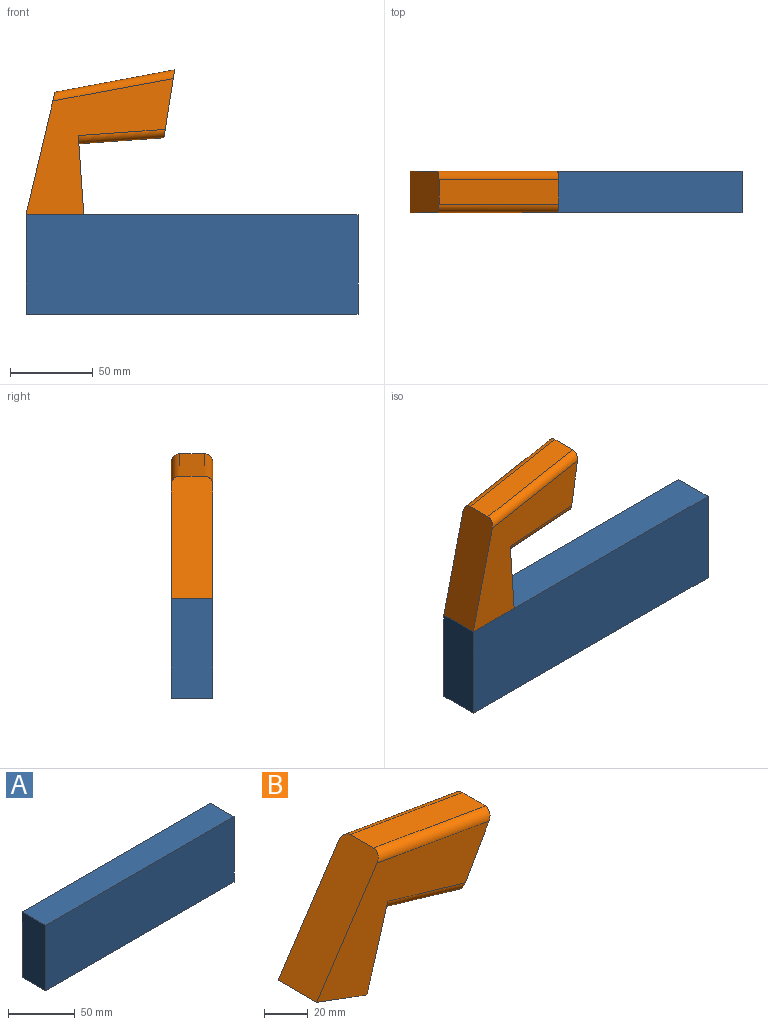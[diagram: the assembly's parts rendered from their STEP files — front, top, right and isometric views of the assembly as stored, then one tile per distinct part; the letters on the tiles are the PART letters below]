
ASSEMBLY  parts=2 mates=1
PART A: 6 faces, bbox 200x25x60 mm
  f0: plane 200x25mm, normal (0,0,1), area 5000mm2, adj f1,f3,f4,f5
  f1: plane 60x25mm, normal (-1,0,0), area 1500mm2, adj f0,f2,f4,f5
  f2: plane 200x25mm, normal (0,0,-1), area 5000mm2, adj f1,f3,f4,f5
  f3: plane 60x25mm, normal (1,0,0), area 1500mm2, adj f0,f2,f4,f5
  f4: plane 200x60mm, normal (0,-1,0), area 12000mm2, adj f0,f1,f2,f3
  f5: plane 200x60mm, normal (0,1,0), area 12000mm2, adj f0,f1,f2,f3
PART B: 12 faces, bbox 114.3x25x75.6 mm
  f0: plane 63.08x42.05mm, normal (-0.83,0,0.55), area 1883.5mm2, adj f1,f5,f6,f7,f9,f11
  f1: plane 32.64x25mm, normal (-0.35,0,-0.94), area 870.5mm2, adj f0,f2,f6,f7
  f2: plane 45.82x25mm, normal (0.96,0,-0.28), area 1079.6mm2, adj f1,f3,f6,f7,f8,f10
  f3: plane 49.28x15mm, normal (-0.28,0,-0.96), area 770.3mm2, adj f2,f4,f8,f10
  f4: plane 36.14x25mm, normal (0.87,0,-0.49), area 1014.7mm2, adj f3,f5,f6,f7,f8,f9,f10,f11
  f5: plane 72.28x15mm, normal (0.17,0,0.99), area 1100.2mm2, adj f0,f4,f9,f11
  f6: plane 111.72x70.64mm, normal (0,-1,0), area 3172.2mm2, adj f0,f1,f2,f4,f10,f11
  f7: plane 111.72x70.64mm, normal (0,1,0), area 3172.2mm2, adj f0,f1,f2,f4,f8,f9
  f8: cylinder r=5mm len=51.8mm, axis (0.96,0,-0.28), area 406.6mm2, adj f2,f3,f4,f7
  f9: cylinder r=5mm len=75.31mm, axis (-0.99,0,0.17), area 577.3mm2, adj f0,f4,f5,f7
  f10: cylinder r=5mm len=51.8mm, axis (-0.96,0,0.28), area 406.6mm2, adj f2,f3,f4,f6
  f11: cylinder r=5mm len=75.31mm, axis (0.99,0,-0.17), area 577.3mm2, adj f0,f4,f5,f6
PLACE A t=(58.4,12.5,-166.33)mm
PLACE B rot(axis=(0,-1,0),20.4deg) t=(-145.38,12.5,-93.93)mm
MATE fastened B.f1 <-> A.f0  axis (0,0,-1) through (-100,0,0)mm
